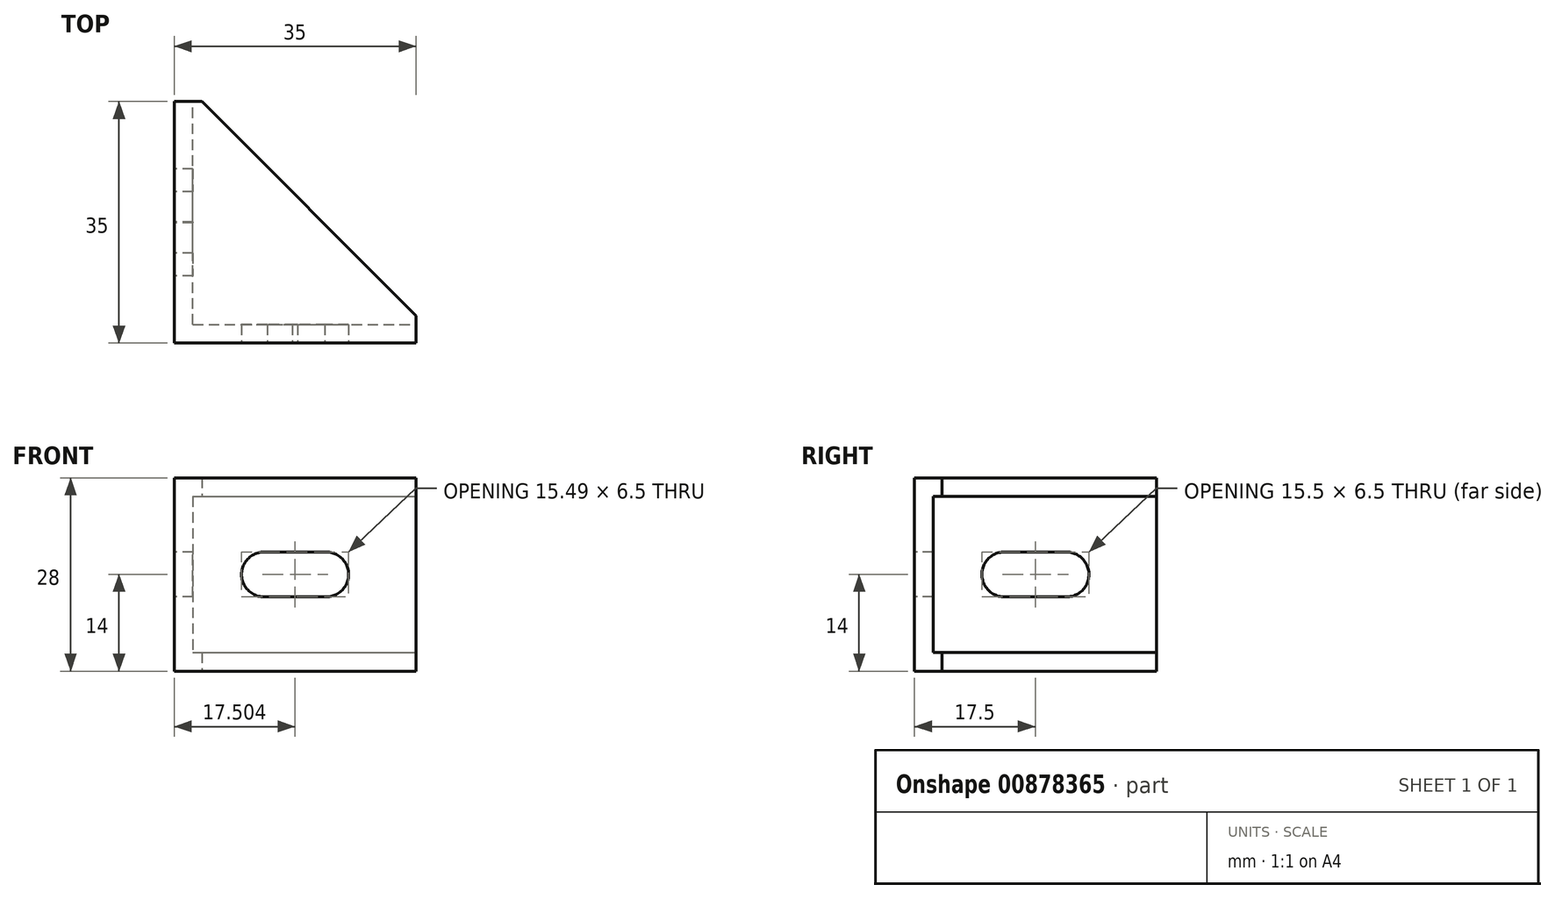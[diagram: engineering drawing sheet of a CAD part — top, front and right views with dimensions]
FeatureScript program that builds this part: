
annotation { "Feature Type Name" : "Feature", "Feature Type Description" : "" }
export const myFeature = defineFeature(function(context is Context, id is Id, definition is map)
    precondition{}
    {
        {
            var Q0;
            Q0=qCreatedBy(makeId("Top.planeOp"),FACE);
            var sketch = newSketch(context, id + "F0", { "sketchPlane" : qUnion([Q0])});
            skLineSegment(sketch, "E0", {"start": v(0, 0) * mm, "end": v(0, 35) * mm});
            skLineSegment(sketch, "E1", {"start": v(0, 0) * mm, "end": v(35, 0) * mm});
            skLineSegment(sketch, "E2", {"start": v(35, 0) * mm, "end": v(35, 4) * mm});
            skLineSegment(sketch, "E3", {"start": v(0, 35) * mm, "end": v(4, 35) * mm});
            skLineSegment(sketch, "E4", {"start": v(4, 35) * mm, "end": v(35, 4) * mm});
            skSolve(sketch);
        }
        {
            var Q0;
            Q0=makeQuery(id+"F0.imprint","IMPRINT",FACE,{"disambiguationData":[TD([[makeQuery(id+"F0.imprint","IMPRINT",EDGE,{"derivedFrom":sQuery(id+"F0.wireOp",EDGE,"E0")}),-1.0]])]});
            extrude(context, id + "F1", {"entities" : qUnion([Q0]), "depth" : 28 * mm, "offsetDistance" : 25 * mm});
        }
        {
            var Q0;
            Q0=makeQuery(id+"F1.opExtrude","SWEPT_FACE",FACE,{"disambiguationData":[OSD([sQuery(id+"F0.wireOp",EDGE,"E4")])]});
            var Q1;
            Q1=makeQuery(id+"F1.opExtrude","SWEPT_FACE",FACE,{"disambiguationData":[OSD([sQuery(id+"F0.wireOp",EDGE,"E3")])]});
            var Q2;
            Q2=makeQuery(id+"F1.opExtrude","SWEPT_FACE",FACE,{"disambiguationData":[OSD([sQuery(id+"F0.wireOp",EDGE,"E2")])]});
            shell(context, id + "F2", {"entities" : qUnion([Q0, Q1, Q2]), "thickness" : 2.7 * mm});
        }
        {
            var Q0;
            Q0=makeQuery(id+"F1.opExtrude","SWEPT_FACE",FACE,{"disambiguationData":[OSD([sQuery(id+"F0.wireOp",EDGE,"E0")])]});
            var sketch = newSketch(context, id + "F3", { "sketchPlane" : qUnion([Q0])});
            skArc(sketch, "E5", {"start": v(-17.54, 10.75) * mm, "mid": v(-17.5, 10.75) * mm, "end": v(-17.46, 10.75) * mm});
            skPoint(sketch, "E5.centerSnap0", {"position": v(-17.5, 0) * mm});
            skPoint(sketch, "E5.centerSnap1", {"position": v(-35, 14) * mm});
            skLineSegment(sketch, "E6", {"start": v(-17.5, 14) * mm, "end": v(-25.25, 14) * mm});
            skLineSegment(sketch, "E7", {"start": v(-25.25, 14) * mm, "end": v(-22, 14) * mm});
            skArc(sketch, "E8", {"start": v(-22, 17.25) * mm, "mid": v(-25.25, 13.98) * mm, "end": v(-21.96, 10.75) * mm});
            skLineSegment(sketch, "E9", {"start": v(-17.5, 14) * mm, "end": v(-9.75, 14) * mm});
            skLineSegment(sketch, "E10", {"start": v(-9.75, 14) * mm, "end": v(-13, 14) * mm});
            skArc(sketch, "E11", {"start": v(-13.04, 10.75) * mm, "mid": v(-9.75, 14.02) * mm, "end": v(-13.07, 17.25) * mm});
            skLineSegment(sketch, "E12", {"start": v(-13.07, 17.25) * mm, "end": v(-22, 17.25) * mm});
            skLineSegment(sketch, "E13", {"start": v(-12.96, 10.75) * mm, "end": v(-22.04, 10.75) * mm});
            skSolve(sketch);
        }
        {
            var Q0;
            Q0 = qSketchRegion(id + "F3", true);
            extrude(context, id + "F4", {"entities" : qUnion([Q0]), "operationType" : NewBodyOperationType.REMOVE, "oppositeDirection" : true, "depth" : 25 * mm, "offsetDistance" : 25 * mm});
        }
        {
            var Q0;
            Q0=makeQuery(id+"F1.opExtrude","SWEPT_FACE",FACE,{"disambiguationData":[OSD([sQuery(id+"F0.wireOp",EDGE,"E1")])]});
            var sketch = newSketch(context, id + "F5", { "sketchPlane" : qUnion([Q0])});
            skPoint(sketch, "E14.centerSnap0", {"position": v(35, 14) * mm});
            skPoint(sketch, "E14.centerSnap1", {"position": v(17.5, 28) * mm});
            skArc(sketch, "E15", {"start": v(21.79, 10.76) * mm, "mid": v(25.25, 13.9) * mm, "end": v(22, 17.25) * mm});
            skArc(sketch, "E16", {"start": v(13.02, 17.25) * mm, "mid": v(9.76, 13.76) * mm, "end": v(13.5, 10.79) * mm});
            skLineSegment(sketch, "E17", {"start": v(12.98, 17.25) * mm, "end": v(22, 17.25) * mm});
            skLineSegment(sketch, "E18", {"start": v(21.79, 10.76) * mm, "end": v(12.47, 10.8) * mm});
            skArc(sketch, "E19.trimOffspring", {"start": v(17.51, 17.25) * mm, "mid": v(17.5, 17.25) * mm, "end": v(17.49, 17.25) * mm});
            skArc(sketch, "E20.trimOffspring", {"start": v(17.1, 10.78) * mm, "mid": v(17.49, 10.75) * mm, "end": v(17.88, 10.77) * mm});
            skSolve(sketch);
        }
        {
            var Q0;
            Q0 = qSketchRegion(id + "F5", true);
            extrude(context, id + "F6", {"entities" : qUnion([Q0]), "operationType" : NewBodyOperationType.REMOVE, "oppositeDirection" : true, "depth" : 25 * mm, "offsetDistance" : 25 * mm});
        }
    });
